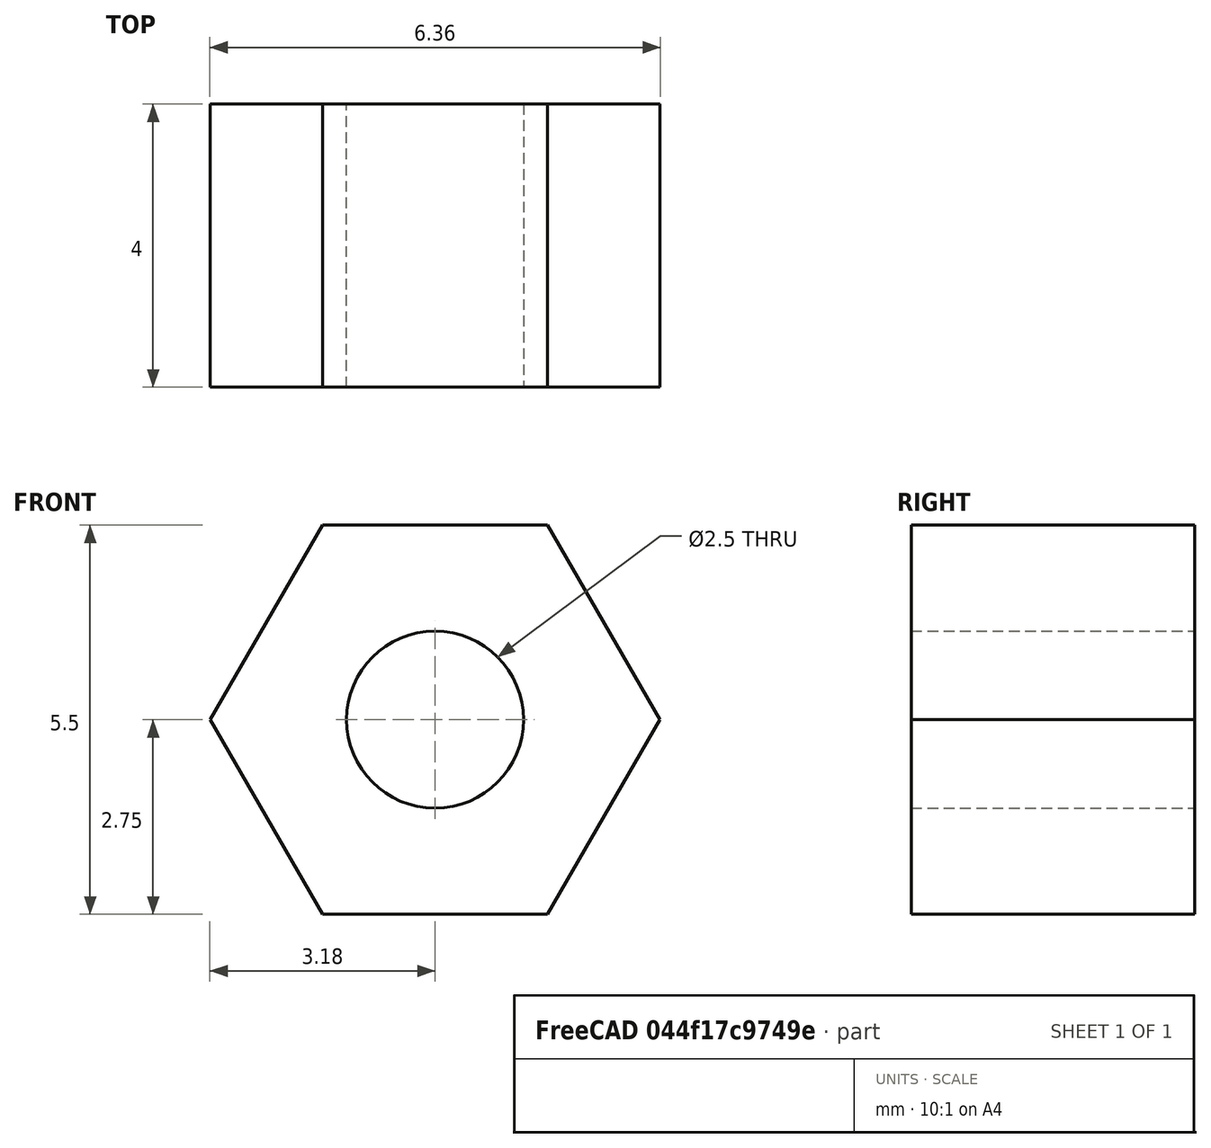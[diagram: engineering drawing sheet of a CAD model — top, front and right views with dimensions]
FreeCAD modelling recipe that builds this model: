
FCSTD DOCUMENT  (FreeCAD 0.21R33771 (Git))
Label: espacador
License: All rights reserved
LicenseURL: https://en.wikipedia.org/wiki/All_rights_reserved
objects: Sketcher::SketchObject×1, PartDesign::Pad×1, PartDesign::Body×1
note: 4 computed .brp shape members not serialized (recipe doc carries the construction recipe); baked Part::Feature solids carry a one-line shape summary decoded from their .brp

FEATURE [Sketcher::SketchObject] Sketch
  FullyConstrained = true
  MapMode = 5
  Placement = pos=(0,0,0) rot=(1,0,0;1.5708rad)
  Support = -> [XZ_Plane]
  sketch-geometry (12):
    g0: LineSegment StartX=-1.58771 StartY=-2.75 StartZ=0 EndX=1.58771 EndY=-2.75 EndZ=0
    g1: LineSegment StartX=1.58771 StartY=-2.75 StartZ=0 EndX=3.17543 EndY=-1.82e-14 EndZ=0
    g2: LineSegment StartX=3.17543 StartY=-1.82e-14 StartZ=0 EndX=1.58771 EndY=2.75 EndZ=0
    g3: LineSegment StartX=1.58771 StartY=2.75 StartZ=0 EndX=-1.58771 EndY=2.75 EndZ=0
    g4: LineSegment StartX=-1.58771 StartY=2.75 StartZ=0 EndX=-3.17543 EndY=4.9e-15 EndZ=0
    g5: LineSegment StartX=-3.17543 StartY=4.7e-15 StartZ=0 EndX=-1.58771 EndY=-2.75 EndZ=0
    g6: Circle CenterX=0 CenterY=0 CenterZ=0 NormalX=0 NormalY=0 NormalZ=1 AngleXU=0 Radius=3.17543
    g7: Circle CenterX=0 CenterY=0 CenterZ=0 NormalX=0 NormalY=0 NormalZ=1 AngleXU=0 Radius=1.25
    g8: LineSegment StartX=-1.25 StartY=1.25 StartZ=0 EndX=1.25 EndY=1.25 EndZ=0
    g9: LineSegment StartX=1.25 StartY=1.25 StartZ=0 EndX=1.25 EndY=-1.25 EndZ=0
    g10: LineSegment StartX=1.25 StartY=-1.25 StartZ=0 EndX=-1.25 EndY=-1.25 EndZ=0
    g11: LineSegment StartX=-1.25 StartY=-1.25 StartZ=0 EndX=-1.25 EndY=1.25 EndZ=0
  constraints (30):
    c: Coincident(g0,g1)
    c: Coincident(g1,g2)
    c: Coincident(g2,g3)
    c: Coincident(g3,g4)
    c: Coincident(g4,g5)
    c: Coincident(g5,g0)
    c: Equal(g0, g1-g5) x5
    c: PointOnObject(g0,g6)
    c: PointOnObject(g1,g6)
    c: PointOnObject(g2,g6)
    c: PointOnObject(g3,g6)
    c: PointOnObject(g4,g6)
    c: PointOnObject(g5,g6)
    c: Coincident(g6,g-1)
    c: Horizontal(g0)
    c: Coincident(g7,g6)
    c: Coincident(g8,g9)
    c: Coincident(g9,g10)
    c: Coincident(g10,g11)
    c: Coincident(g11,g8)
    c: Horizontal(g8)
    c: Horizontal(g10)
    c: Vertical(g9)
    c: Vertical(g11)
    c: Tangent(g8,g7)
    c: Tangent(g7,g11)
    c: Tangent(g10,g7)
    c: Tangent(g9,g7)
    c: Diameter(g7) = 2.5
    c: DistanceY(g8,g2) = 1.5
FEATURE [PartDesign::Pad] Pad
  Direction = (0,-1,2e-16)
  Length = 4
  Length2 = 10
  Placement = pos=(0,0,0) rot=(1,0,0;1.5708rad)
  Profile = -> Sketch
  ReferenceAxis = -> Sketch [N_Axis]
  Type = 0
FEATURE [PartDesign::Body] Body
  Group = -> [Sketch,Pad]
  Origin = -> Origin
  Tip = -> Pad
